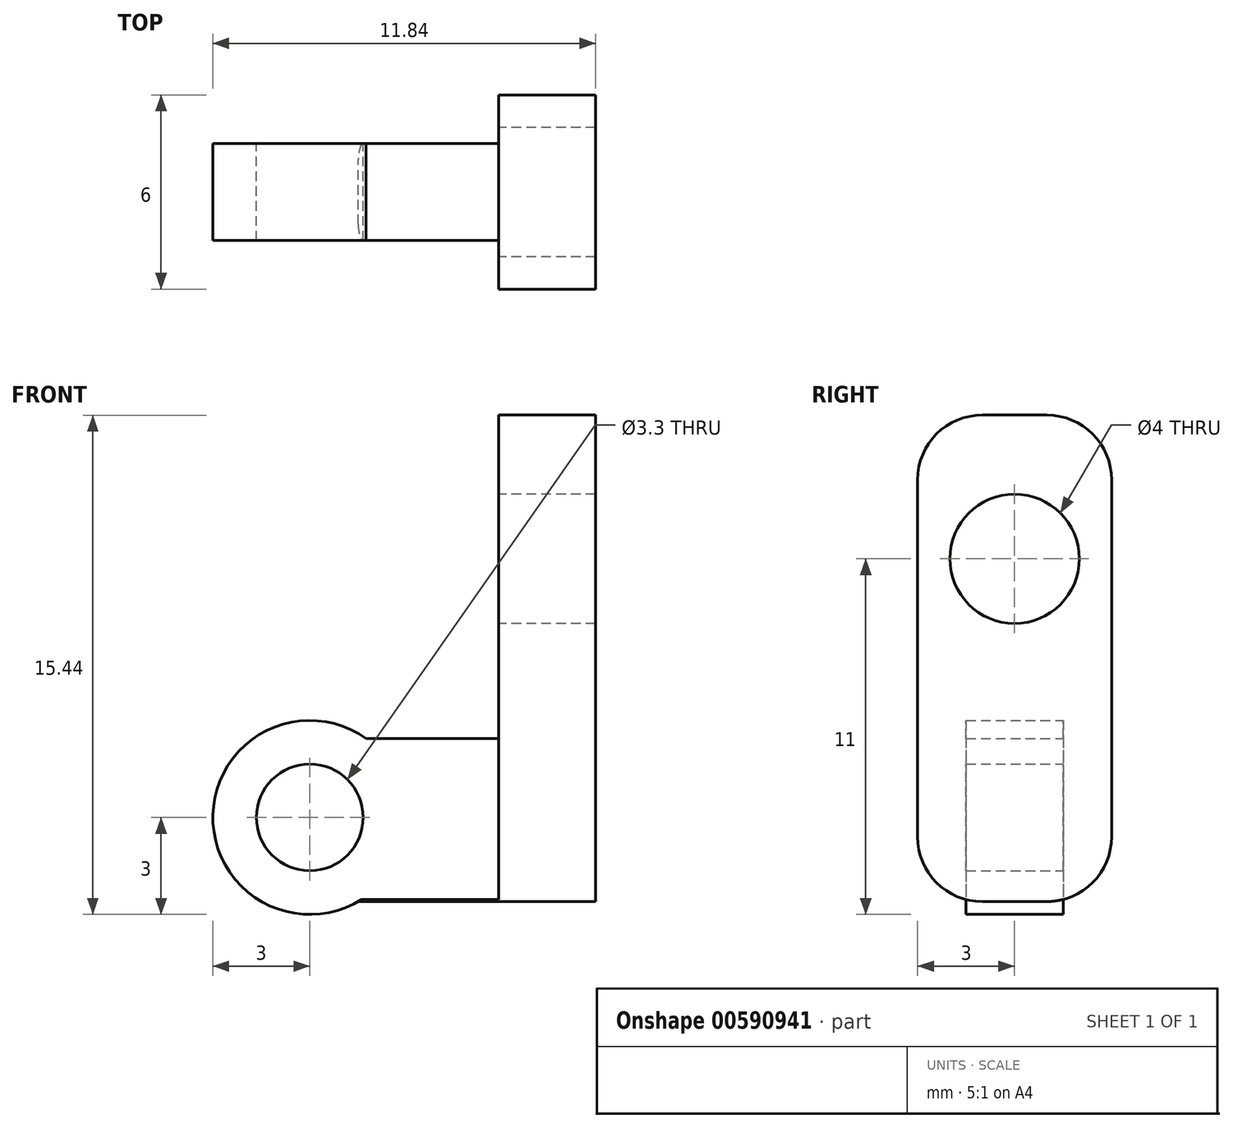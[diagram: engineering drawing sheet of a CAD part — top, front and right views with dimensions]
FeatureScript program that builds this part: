
annotation { "Feature Type Name" : "Feature", "Feature Type Description" : "" }
export const myFeature = defineFeature(function(context is Context, id is Id, definition is map)
    precondition{}
    {
        {
            var Q0;
            Q0=qCreatedBy(makeId("Front.planeOp"),FACE);
            var sketch = newSketch(context, id + "F0", { "sketchPlane" : qUnion([Q0])});
            skCircle(sketch, "E0", {"center": v(0, 0) * mm, "radius": 1.65 * mm});
            skCircle(sketch, "E1.0", {"center": v(0, 0) * mm, "radius": 3 * mm});
            skSolve(sketch);
        }
        {
            var Q0;
            Q0 = qSketchRegion(id + "F0", true);
            extrude(context, id + "F1", {"entities" : qUnion([Q0]), "depth" : 1.5 * mm, "offsetDistance" : 25 * mm, "hasSecondDirection" : true, "secondDirectionOppositeDirection" : true, "secondDirectionDepth" : 1.5 * mm});
        }
        {
            var Q0;
            Q0=qCreatedBy(makeId("Front.planeOp"),FACE);
            var sketch = newSketch(context, id + "F2", { "sketchPlane" : qUnion([Q0])});
            skLineSegment(sketch, "E2", {"start": v(1.74, 2.44) * mm, "end": v(7.74, 2.44) * mm});
            skLineSegment(sketch, "E3", {"start": v(7.74, 2.44) * mm, "end": v(7.74, -2.6) * mm});
            skLineSegment(sketch, "E4", {"start": v(7.74, -2.6) * mm, "end": v(1.5, -2.6) * mm});
            skCircle(sketch, "E5.3", {"center": v(0, 0) * mm, "radius": 3 * mm});
            skSolve(sketch);
        }
        {
            var Q0;
            {var subQ0=sQuery(id+"F2.wireOp",EDGE,"E2");Q0=makeQuery(id+"F2.imprint","IMPRINT",FACE,{"disambiguationData":[TD([[makeQuery(id+"F2.imprint","IMPRINT",EDGE,{"derivedFrom":subQ0}),-1.0]])]});}
            extrude(context, id + "F3", {"entities" : qUnion([Q0]), "operationType" : NewBodyOperationType.ADD, "depth" : 1.5 * mm, "offsetDistance" : 25 * mm, "hasSecondDirection" : true, "secondDirectionOppositeDirection" : true, "secondDirectionDepth" : 1.5 * mm});
        }
        {
            var Q0;
            Q0=qCreatedBy(makeId("Front.planeOp"),FACE);
            var sketch = newSketch(context, id + "F4", { "sketchPlane" : qUnion([Q0])});
            skLineSegment(sketch, "E6.bottom", {"start": v(8.84, -2.6) * mm, "end": v(5.84, -2.6) * mm});
            skLineSegment(sketch, "E6.top", {"start": v(8.84, 12.44) * mm, "end": v(5.84, 12.44) * mm});
            skLineSegment(sketch, "E6.left", {"start": v(8.84, -2.6) * mm, "end": v(8.84, 12.44) * mm});
            skLineSegment(sketch, "E6.right", {"start": v(5.84, -2.6) * mm, "end": v(5.84, 12.44) * mm});
            skSolve(sketch);
        }
        {
            var Q0;
            Q0=makeQuery(id+"F4.imprint","IMPRINT",FACE,{"disambiguationData":[TD([[makeQuery(id+"F4.imprint","IMPRINT",EDGE,{"derivedFrom":sQuery(id+"F4.wireOp",EDGE,"E6.bottom")}),-1.0]])]});
            extrude(context, id + "F5", {"entities" : qUnion([Q0]), "operationType" : NewBodyOperationType.ADD, "depth" : 3 * mm, "offsetDistance" : 25 * mm, "hasSecondDirection" : true, "secondDirectionOppositeDirection" : true, "secondDirectionDepth" : 3 * mm});
        }
        {
            var Q0;
            Q0=makeQuery(id+"F5.opExtrude","SWEPT_FACE",FACE,{"disambiguationData":[OSD([sQuery(id+"F4.wireOp",EDGE,"E6.right")])]});
            var sketch = newSketch(context, id + "F6", { "sketchPlane" : qUnion([Q0])});
            skCircle(sketch, "E7", {"center": v(0, 8) * mm, "radius": 2 * mm});
            skSolve(sketch);
        }
        {
            var Q0;
            Q0=makeQuery(id+"F6.imprint","IMPRINT",FACE,{"disambiguationData":[TD([[makeQuery(id+"F6.imprint","IMPRINT",EDGE,{"derivedFrom":sQuery(id+"F6.wireOp",EDGE,"E7")}),1.0]])]});
            extrude(context, id + "F7", {"entities" : qUnion([Q0]), "operationType" : NewBodyOperationType.REMOVE, "oppositeDirection" : true, "depth" : 25 * mm, "offsetDistance" : 25 * mm});
        }
        {
            var Q0;
            Q0=makeQuery(id+"F5.opExtrude","CAP_EDGE",EDGE,{"disambiguationData":[OSD([sQuery(id+"F4.wireOp",EDGE,"E6.top")])],"isStart":false});
            var Q1;
            Q1=makeQuery(id+"F5.opExtrude","CAP_EDGE",EDGE,{"disambiguationData":[OSD([sQuery(id+"F4.wireOp",EDGE,"E6.top")])],"isStart":true});
            var Q2;
            Q2=makeQuery(id+"F5.opExtrude","CAP_EDGE",EDGE,{"disambiguationData":[OSD([sQuery(id+"F4.wireOp",EDGE,"E6.bottom")])],"isStart":false});
            var Q3;
            Q3=makeQuery(id+"F5.opExtrude","CAP_EDGE",EDGE,{"disambiguationData":[OSD([sQuery(id+"F4.wireOp",EDGE,"E6.bottom")])],"isStart":true});
            fillet(context, id + "F8", {"entities" : qUnion([Q0, Q1, Q2, Q3]), "radius" : 2 * mm, "tangentPropagation" : true, "allowEdgeOverflow" : false});
        }
    });
